# Revit family: X-194PLAIN
name_source: partatom
category: Plumbing Fixtures
revit_build: Autodesk Revit Architecture 2012 (Build: 20110309_2315(x64)
units: mm (PartAtom-declared; Revit-internal decimal feet)

## types (1)
- X-194 PLAIN
    Angle regulating valve 232-10. Headpart clockwise closing = S-21-1CLOCK
    Assembly Code = D2010
    CW Connection = Yes
    CWFU = 0
    Connection tubes C-M10X1/2. Aerator = C-M22X1-FLEX
    Cost = 0 $
    Default Elevation = 0' - 0"
    Description = One hole basin mixer with swivel outlet and angle valves.
    HW Connection = Yes
    HWFU = 0
    Headpart complete = P-21-1X
    Keynote = Basin mixer with aerated swivel outlet.
    Manufacturer = COBRA
    Material = Chrome-Polished
    Model = X-194 PLAIN
    Range = Ixion
    Type Comments = SANS 226
    URL = http://www.cobra.co.za
    Vent Connection = No
    WFU = 0
    Waste Connection = Yes

## geometry (parser evidence)
native form markers: Blend x2
no freeform markers — native parametric forms only
